FCSTD DOCUMENT  (FreeCAD 1.0R39319 (Git))
Label: PICON-OF-interno-esterno
License: All rights reserved
LicenseURL: https://en.wikipedia.org/wiki/All_rights_reserved
objects: Sketcher::SketchObject×1, PartDesign::Body×1
note: 3 computed .brp shape members not serialized (recipe doc carries the construction recipe); baked Part::Feature solids carry a one-line shape summary decoded from their .brp

FEATURE [Sketcher::SketchObject] Sketch
  ArcFitTolerance = 1e-06
  AttachmentSupport = -> [XZ_Plane]
  FullyConstrained = true
  MakeInternals = false
  MapMode = 5
  Placement = pos=(0,0,0) rot=(1,0,0;1.5708rad)
  sketch-geometry (75):
    g0: LineSegment StartX=0 StartY=0 StartZ=0 EndX=-57.2 EndY=0 EndZ=0
    g1: LineSegment StartX=-57.2 StartY=0 StartZ=0 EndX=-57.2 EndY=-10.4 EndZ=0
    g2: LineSegment StartX=-57.2 StartY=-10.4 StartZ=0 EndX=-82.8 EndY=-10.4 EndZ=0
    g3: LineSegment StartX=-82.8 StartY=-10.4 StartZ=0 EndX=-82.8 EndY=3.2 EndZ=0
    g4: LineSegment StartX=-82.8 StartY=3.2 StartZ=0 EndX=-93.6 EndY=3.2 EndZ=0
    g5: LineSegment StartX=-93.6 StartY=3.2 StartZ=0 EndX=-93.6 EndY=18 EndZ=0
    g6: LineSegment StartX=-93.6 StartY=18 StartZ=0 EndX=-141.6 EndY=18 EndZ=0
    g7: LineSegment StartX=-141.6 StartY=18 StartZ=0 EndX=-174.232 EndY=-82.4316 EndZ=0
    g8: LineSegment StartX=-174.232 StartY=-82.4316 StartZ=0 EndX=-218.232 EndY=-82.4316 EndZ=0
    g9: LineSegment StartX=-224.632 StartY=-62.4316 StartZ=0 EndX=-207.531 EndY=-15.4469 EndZ=0
    g10: LineSegment StartX=-204.528 StartY=27.6697 StartZ=0 EndX=-199.861 EndY=40.4914 EndZ=0
    g11: LineSegment StartX=-199.861 StartY=40.4914 StartZ=0 EndX=-197.061 EndY=40.4914 EndZ=0
    g12: LineSegment StartX=-197.061 StartY=40.4914 StartZ=0 EndX=-197.061 EndY=42.8914 EndZ=0
    g13: LineSegment StartX=-197.061 StartY=42.8914 StartZ=0 EndX=-194.261 EndY=42.8914 EndZ=0
    g14: LineSegment StartX=-194.261 StartY=42.8914 StartZ=0 EndX=-194.535 EndY=42.1397 EndZ=0
    g15: LineSegment StartX=-194.535 StartY=42.1397 StartZ=0 EndX=-193.031 EndY=41.5924 EndZ=0
    g16: LineSegment StartX=-193.031 StartY=41.5924 StartZ=0 EndX=-191.663 EndY=45.3512 EndZ=0
    g17: LineSegment StartX=-191.663 StartY=45.3512 StartZ=0 EndX=-190.536 EndY=44.9408 EndZ=0
    g18: LineSegment StartX=-190.536 StartY=44.9408 StartZ=0 EndX=-185.747 EndY=58.0965 EndZ=0
    g19: LineSegment StartX=-185.747 StartY=58.0965 StartZ=0 EndX=-185.747 EndY=62.0965 EndZ=0
    g20: LineSegment StartX=-185.747 StartY=62.0965 StartZ=0 EndX=-183.832 EndY=67.3588 EndZ=0
    g21: LineSegment StartX=-183.832 StartY=67.3588 StartZ=0 EndX=-180.232 EndY=67.3588 EndZ=0
    g22: LineSegment StartX=-180.232 StartY=67.3588 StartZ=0 EndX=-180.232 EndY=63.7588 EndZ=0
    g23: LineSegment StartX=-180.232 StartY=63.7588 StartZ=0 EndX=-181.6 EndY=60 EndZ=0
    g24: LineSegment StartX=-181.6 StartY=60 StartZ=0 EndX=-181.6 EndY=41.2 EndZ=0
    g25: LineSegment StartX=-181.6 StartY=41.2 StartZ=0 EndX=-100.8 EndY=41.2 EndZ=0
    g26: LineSegment StartX=-100.8 StartY=41.2 StartZ=0 EndX=-100.8 EndY=43.2 EndZ=0
    g27: LineSegment StartX=-100.8 StartY=43.2 StartZ=0 EndX=-36 EndY=43.2 EndZ=0
    g28: LineSegment StartX=-36 StartY=43.2 StartZ=0 EndX=-36 EndY=48 EndZ=0
    g29: LineSegment StartX=-36 StartY=48 StartZ=0 EndX=0 EndY=48 EndZ=0
    g30: LineSegment StartX=0 StartY=48 StartZ=0 EndX=0 EndY=0 EndZ=0
    g31: LineSegment StartX=-224.632 StartY=24.184 StartZ=0 EndX=-224.632 EndY=25.2301 EndZ=0
    g32: LineSegment StartX=-223.278 StartY=26.584 StartZ=0 EndX=-206.078 EndY=26.584 EndZ=0
    g33: LineSegment StartX=-222.232 StartY=22.584 StartZ=0 EndX=-223.032 EndY=22.584 EndZ=0
    g34: GeomPoint [constr] X=-218.232 Y=-82.4316 Z=0
    g35: GeomPoint [constr] X=-224.632 Y=-62.4316 Z=0
    g36: BSplineCurve PolesCount=4 KnotsCount=2 Degree=3 IsPeriodic=0
    g37-g40: Circle [constr] x4 (B-spline internal-alignment scaffolding for g36; pole/knot coordinates omitted)
    g41: GeomPoint [constr] X=-207.531 Y=-15.4469 Z=0
    g42: GeomPoint [constr] X=-202.534 Y=0 Z=0
    g43: GeomPoint [constr] X=-222.232 Y=22.584 Z=0
    g44: BSplineCurve PolesCount=4 KnotsCount=2 Degree=3 IsPeriodic=0
    g45-g48: Circle [constr] x4 (B-spline internal-alignment scaffolding for g44; pole/knot coordinates omitted)
    g49: ArcOfCircle CenterX=-223.278 CenterY=25.2301 CenterZ=0 NormalX=0 NormalY=0 NormalZ=1 AngleXU=0 Radius=1.35384 StartAngle=1.5708 EndAngle=3.14159
    g50: GeomPoint [constr] X=-224.632 Y=26.584 Z=0
    g51: ArcOfCircle CenterX=-223.032 CenterY=24.184 CenterZ=0 NormalX=0 NormalY=0 NormalZ=1 AngleXU=0 Radius=1.6 StartAngle=3.14159 EndAngle=4.71239
    g52: GeomPoint [constr] X=-224.632 Y=22.584 Z=0
    g53: ArcOfCircle CenterX=-206.078 CenterY=28.234 CenterZ=0 NormalX=0 NormalY=0 NormalZ=1 AngleXU=0 Radius=1.65 StartAngle=4.71239 EndAngle=5.93412
    g54: GeomPoint [constr] X=-204.923 Y=26.584 Z=0
    g55: LineSegment StartX=-4 StartY=6 StartZ=0 EndX=-4 EndY=36.4 EndZ=0
    g56: LineSegment StartX=-4 StartY=36.4 StartZ=0 EndX=-185.2 EndY=36.4 EndZ=0
    g57: LineSegment StartX=-185.2 StartY=36.4 StartZ=0 EndX=-191.311 EndY=19.6103 EndZ=0
    g58: LineSegment StartX=-191.311 StartY=19.6103 StartZ=0 EndX=-190.711 EndY=15.24 EndZ=0
    g59: LineSegment StartX=-215.322 StartY=-78.4316 StartZ=0 EndX=-177.142 EndY=-78.4316 EndZ=0
    g60: LineSegment StartX=-177.142 StartY=-78.4316 StartZ=0 EndX=-144.51 EndY=22 EndZ=0
    g61: LineSegment StartX=-144.51 StartY=22 StartZ=0 EndX=-86.91 EndY=22 EndZ=0
    g62: LineSegment StartX=-86.91 StartY=22 StartZ=0 EndX=-86.91 EndY=10.4 EndZ=0
    g63: LineSegment StartX=-86.91 StartY=10.4 StartZ=0 EndX=-77.31 EndY=10.4 EndZ=0
    g64: LineSegment StartX=-77.31 StartY=10.4 StartZ=0 EndX=-77.31 EndY=6 EndZ=0
    g65: LineSegment StartX=-77.31 StartY=6 StartZ=0 EndX=-4 EndY=6 EndZ=0
    g66: LineSegment StartX=-190.711 StartY=15.24 StartZ=0 EndX=-203.814 EndY=-16.924 EndZ=0
    g67: LineSegment StartX=-203.814 StartY=-16.924 StartZ=0 EndX=-220.915 EndY=-63.9087 EndZ=0
    g68: GeomPoint [constr] X=-215.322 Y=-78.4316 Z=0
    g69: GeomPoint [constr] X=-220.915 Y=-63.9087 Z=0
    g70: BSplineCurve PolesCount=4 KnotsCount=2 Degree=3 IsPeriodic=0
    g71-g74: Circle [constr] x4 (B-spline internal-alignment scaffolding for g70; pole/knot coordinates omitted)
  constraints (205):
    c: Coincident(g-1,g0)
    c: PointOnObject(g0,g-1)
    c: Coincident(g0,g1)
    c: Vertical(g1)
    c: Coincident(g1,g2)
    c: Horizontal(g2)
    c: Coincident(g2,g3)
    c: Vertical(g3)
    c: Coincident(g3,g4)
    c: Coincident(g4,g5)
    c: Vertical(g5)
    c: Coincident(g5,g6)
    c: Horizontal(g6)
    c: Coincident(g6,g7)
    c: Coincident(g7,g8)
    c: Horizontal(g8)
    c: Coincident(g10,g11)
    c: Horizontal(g11)
    c: Coincident(g11,g12)
    c: Vertical(g12)
    c: Coincident(g12,g13)
    c: Horizontal(g13)
    c: Coincident(g13,g14)
    c: Coincident(g14,g15)
    c: Coincident(g15,g16)
    c: Coincident(g16,g17)
    c: Coincident(g17,g18)
    c: Coincident(g18,g19)
    c: Vertical(g19)
    c: Coincident(g19,g20)
    c: Coincident(g20,g21)
    c: Horizontal(g21)
    c: Coincident(g21,g22)
    c: Vertical(g22)
    c: Coincident(g22,g23)
    c: Coincident(g23,g24)
    c: Vertical(g24)
    c: Coincident(g24,g25)
    c: Horizontal(g25)
    c: Coincident(g25,g26)
    c: Vertical(g26)
    c: Coincident(g26,g27)
    c: Horizontal(g27)
    c: Coincident(g27,g28)
    c: Vertical(g28)
    c: Coincident(g28,g29)
    c: PointOnObject(g29,g-2)
    c: Horizontal(g29)
    c: Coincident(g29,g30)
    c: Coincident(g30,g0)
    c: DistanceY(g30,g30) = 48
    c: DistanceY(g1,g1) = 10.4
    c: DistanceX(g0,g0) = 57.2
    c: DistanceX(g2,g2) = 25.6
    c: Horizontal(g4)
    c: DistanceY(g3,g3) = 13.6
    c: DistanceX(g4,g4) = 10.8
    c: DistanceY(g5,g5) = 14.8
    c: DistanceX(g6,g6) = 48
    c: Angle(g7,g-1) = 1.88496
    c: Distance(g7) = 105.6
    c: DistanceX(g29,g29) = 36
    c: DistanceX(g27,g27) = 64.8
    c: DistanceY(g26,g26) = 2
    c: DistanceY(g28,g28) = 4.8
    c: DistanceX(g25,g25) = 80.8
    c: DistanceY(g24,g24) = 18.8
    c: DistanceY(g22,g22) = 3.6
    c: Distance(g23) = 4
    c: Angle(g-1,g23) = 1.22173
    c: DistanceX(g21,g21) = 3.6
    c: Distance(g20) = 5.6
    c: Angle(g-1,g20) = 1.22173
    c: DistanceY(g19,g19) = 4
    c: Distance(g18) = 14
    c: Angle(g-1,g18) = 1.22173
    c: Distance(g17) = 1.2
    c: Distance(g16) = 4
    c: Angle(g16) = 1.22173
    c: Perpendicular(g18,g17)
    c: Distance(g15) = 1.6
    c: Perpendicular(g16,g15)
    c: Distance(g14) = 0.8
    c: DistanceX(g13,g13) = 2.8
    c: Perpendicular(g15,g14)
    c: DistanceY(g12,g12) = 2.4
    c: DistanceX(g11,g11) = 2.8
    c: Distance(g10,g54) = 14.8
    c: Distance(g9) = 50
    c: Angle(g9,g-1) = 1.91986
    c: DistanceX(g50,g9) = 0
    c: Horizontal(g32)
    c: Vertical(g31)
    c: DistanceY(g52,g50) = 4
    c: InternalAlignment(g34,g36)
    c: InternalAlignment(g35,g36)
    c: InternalAlignment(g37,g36)
    c: Weight(g37) = 1
    c: InternalAlignment(g38,g36)
    c: Equal(g38,g37)
    c: InternalAlignment(g39,g36)
    c: Equal(g39,g37)
    c: InternalAlignment(g40,g36)
    c: Equal(g40,g37)
    c: Coincident(g34,g8)
    c: Coincident(g35,g9)
    c: Horizontal(g33)
    c: InternalAlignment(g41,g44)
    c: PointOnObject(g42,g44)
    c: InternalAlignment(g43,g44)
    c: InternalAlignment(g45,g44)
    c: Weight(g45) = 1
    c: InternalAlignment(g46,g44)
    c: Equal(g46,g45)
    c: InternalAlignment(g47,g44)
    c: Equal(g47,g45)
    c: InternalAlignment(g48,g44)
    c: Equal(g48,g45)
    c: Coincident(g41,g9)
    c: Coincident(g43,g33)
    c: DistanceY(g-1,g42) = 0
    c: DistanceY(g36,g36) = 20
    c: PointOnObject(g50,g32)
    c: PointOnObject(g50,g31)
    c: Tangent(g32,g49) = 1.5708
    c: Tangent(g31,g49) = 1.5708
    c: PointOnObject(g52,g31)
    c: PointOnObject(g52,g33)
    c: Tangent(g31,g51) = 1.5708
    c: Tangent(g33,g51) = 1.5708
    c: PointOnObject(g54,g32)
    c: PointOnObject(g54,g10)
    c: Tangent(g32,g53) = -1.5708
    c: Tangent(g10,g53) = -1.5708
    c: DistanceX(g36,g36) = 6.4
    c: DistanceX(g8,g8) = 44
    c: DistanceX(g32,g32) = 17.2
    c: Angle(g-1,g10) = 1.22173
    c: Radius(g53) = 1.65
    c: Radius(g51) = 1.6
    c: DistanceX(g39,g36) = 3.39805
    c: DistanceY(g39,g36) = 8.82115
    c: DistanceX(g38) = -222.425
    c: DistanceY(g38) = -79.8613
    c: DistanceX(g47) = -198.906
    c: DistanceY(g47) = 19.1595
    c: DistanceX(g46) = -199.347
    c: DistanceY(g46) = -0.819322
    c: Distance(g33) = 0.8
    c: Vertical(g55)
    c: Coincident(g55,g56)
    c: Horizontal(g56)
    c: Coincident(g56,g57)
    c: Coincident(g57,g58)
    c: Coincident(g58,g66)
    c: Horizontal(g59)
    c: Coincident(g59,g60)
    c: Coincident(g60,g61)
    c: Horizontal(g61)
    c: Coincident(g61,g62)
    c: Vertical(g62)
    c: Coincident(g62,g63)
    c: Horizontal(g63)
    c: Coincident(g63,g64)
    c: Vertical(g64)
    c: Coincident(g64,g65)
    c: Coincident(g65,g55)
    c: Horizontal(g65)
    c: DistanceY(g0,g55) = 6
    c: DistanceX(g55,g0) = 4
    c: DistanceY(g55,g25) = 4.8
    c: DistanceX(g56,g56) = 181.2
    c: DistanceX(g61,g61) = 57.6
    c: DistanceY(g6,g60) = 4
    c: DistanceX(g60,g6) = 2.91
    c: Angle(g60,g-1) = 1.88496
    c: DistanceY(g62,g62) = 11.6
    c: DistanceX(g63,g63) = 9.6
    c: DistanceY(g7,g59) = 4
    c: Coincident(g66,g67)
    c: Distance(g67) = 50
    c: Angle(g67,g-1) = 1.91986
    c: DistanceX(g36,g59) = 2.91
    c: Distance(g67,g36) = 4
    c: InternalAlignment(g68,g70)
    c: InternalAlignment(g69,g70)
    c: InternalAlignment(g71,g70)
    c: Weight(g71) = 1
    c: InternalAlignment(g72,g70)
    c: Equal(g72,g71)
    c: InternalAlignment(g73,g70)
    c: Equal(g73,g71)
    c: InternalAlignment(g74,g70)
    c: Equal(g74,g71)
    c: Coincident(g68,g59)
    c: Coincident(g69,g67)
    c: DistanceX(g70) = -220.915
    c: DistanceX(g73) = -221.986
    c: DistanceY(g73) = -68.8844
    c: DistanceX(g72) = -219.406
    c: DistanceY(g72) = -77.4616
    c: Angle(g-1,g57) = 1.22173
    c: DistanceX(g57) = -191.311
    c: DistanceX(g58) = -190.711
    c: DistanceY(g58) = 15.24
FEATURE [PartDesign::Body] Body  label="Corpo"
  AllowCompound = false
  Group = -> [Sketch]
  Origin = -> Origin
